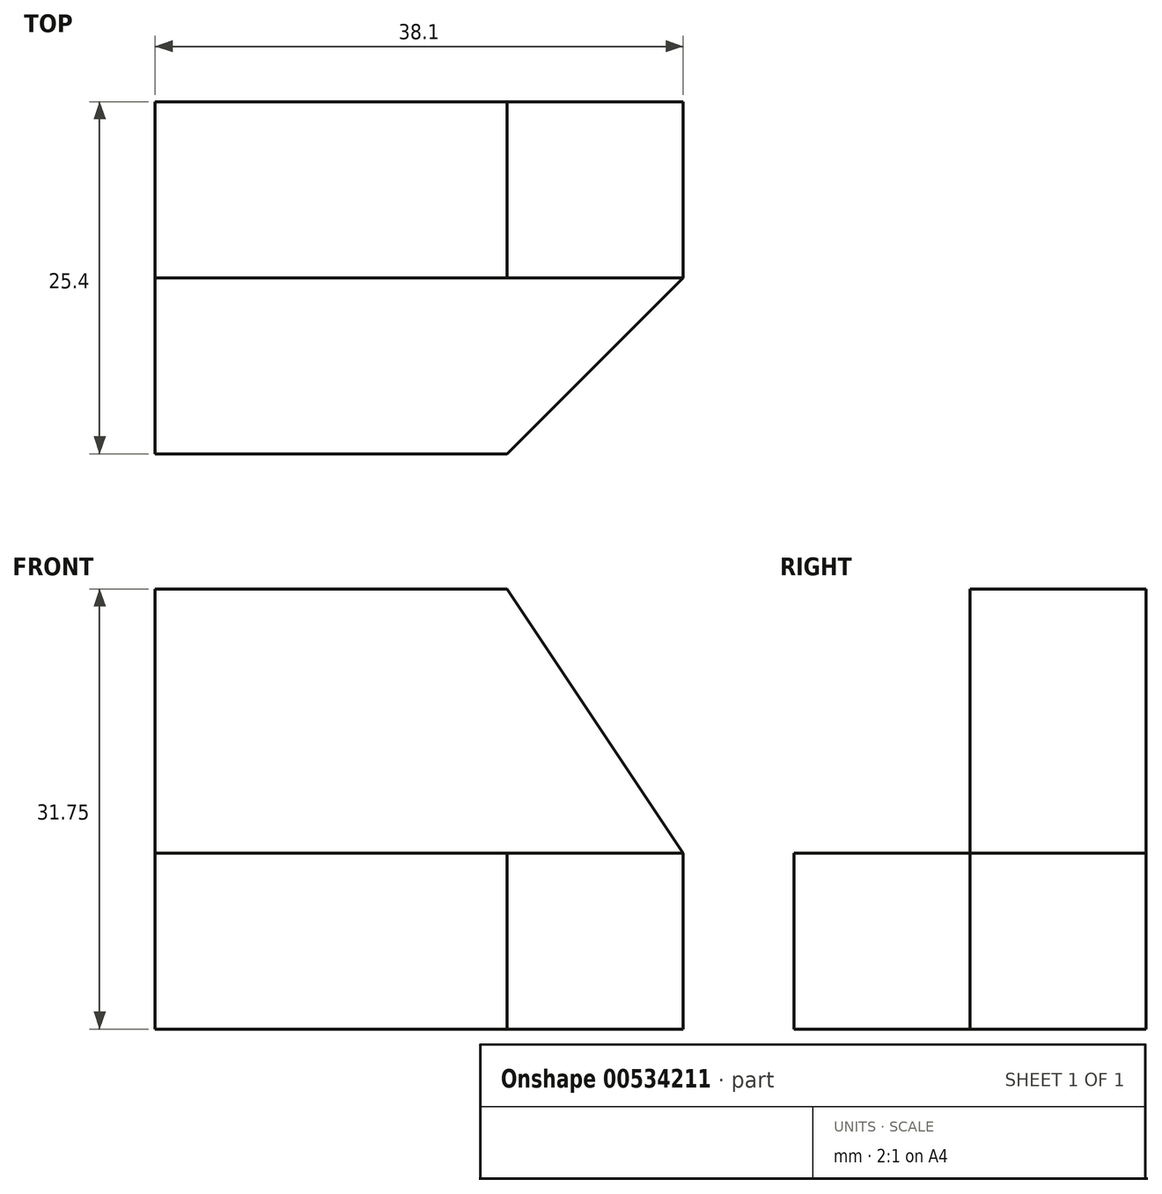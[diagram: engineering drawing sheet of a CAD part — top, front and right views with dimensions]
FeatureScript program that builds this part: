
annotation { "Feature Type Name" : "Feature", "Feature Type Description" : "" }
export const myFeature = defineFeature(function(context is Context, id is Id, definition is map)
    precondition{}
    {
        {
            var Q0;
            Q0=qCreatedBy(makeId("Right.planeOp"),FACE);
            var sketch = newSketch(context, id + "F0", { "sketchPlane" : qUnion([Q0])});
            skLineSegment(sketch, "E0", {"start": v(0, 0) * mm, "end": v(25.4, 0) * mm});
            skLineSegment(sketch, "E1", {"start": v(25.4, 0) * mm, "end": v(25.4, 31.75) * mm});
            skLineSegment(sketch, "E2", {"start": v(25.4, 31.75) * mm, "end": v(12.7, 31.75) * mm});
            skLineSegment(sketch, "E3", {"start": v(12.7, 31.75) * mm, "end": v(12.7, 12.7) * mm});
            skLineSegment(sketch, "E4", {"start": v(12.7, 12.7) * mm, "end": v(0, 12.7) * mm});
            skLineSegment(sketch, "E5", {"start": v(0, 12.7) * mm, "end": v(0, 0) * mm});
            skSolve(sketch);
        }
        {
            var Q0;
            Q0=makeQuery(id+"F0.imprint","IMPRINT",FACE,{"disambiguationData":[TD([[makeQuery(id+"F0.imprint","IMPRINT",EDGE,{"derivedFrom":sQuery(id+"F0.wireOp",EDGE,"E0")}),1.0]])]});
            extrude(context, id + "F1", {"entities" : qUnion([Q0]), "depth" : 38.1 * mm, "offsetDistance" : 25.4 * mm});
        }
        {
            var Q0;
            Q0=makeQuery(id+"F1.opExtrude","SWEPT_FACE",FACE,{"disambiguationData":[OSD([sQuery(id+"F0.wireOp",EDGE,"E4")])]});
            var sketch = newSketch(context, id + "F2", { "sketchPlane" : qUnion([Q0])});
            skLineSegment(sketch, "E6", {"start": v(38.1, 12.7) * mm, "end": v(25.4, 0) * mm});
            skLineSegment(sketch, "E7", {"start": v(25.4, 0) * mm, "end": v(38.1, 0) * mm});
            skLineSegment(sketch, "E8", {"start": v(38.1, 0) * mm, "end": v(38.1, 12.7) * mm});
            skSolve(sketch);
        }
        {
            var Q0;
            Q0=makeQuery(id+"F2.imprint","IMPRINT",FACE,{"disambiguationData":[TD([[makeQuery(id+"F2.imprint","IMPRINT",EDGE,{"derivedFrom":sQuery(id+"F2.wireOp",EDGE,"E6")}),1.0]])]});
            extrude(context, id + "F3", {"entities" : qUnion([Q0]), "operationType" : NewBodyOperationType.REMOVE, "oppositeDirection" : true, "depth" : 12.7 * mm, "offsetDistance" : 25.4 * mm});
        }
        {
            var Q0;
            Q0=makeQuery(id+"F1.opExtrude","SWEPT_FACE",FACE,{"disambiguationData":[OSD([sQuery(id+"F0.wireOp",EDGE,"E3")])]});
            var sketch = newSketch(context, id + "F4", { "sketchPlane" : qUnion([Q0])});
            skLineSegment(sketch, "E9", {"start": v(38.1, 12.7) * mm, "end": v(38.1, 31.75) * mm});
            skLineSegment(sketch, "E10", {"start": v(38.1, 12.7) * mm, "end": v(25.4, 31.75) * mm});
            skLineSegment(sketch, "E11", {"start": v(25.4, 31.75) * mm, "end": v(38.1, 31.75) * mm});
            skSolve(sketch);
        }
        {
            var Q0;
            Q0=makeQuery(id+"F4.imprint","IMPRINT",FACE,{"disambiguationData":[TD([[makeQuery(id+"F4.imprint","IMPRINT",EDGE,{"derivedFrom":sQuery(id+"F4.wireOp",EDGE,"E9")}),-1.0]])]});
            extrude(context, id + "F5", {"entities" : qUnion([Q0]), "operationType" : NewBodyOperationType.REMOVE, "oppositeDirection" : true, "depth" : 12.7 * mm, "offsetDistance" : 25.4 * mm});
        }
    });
